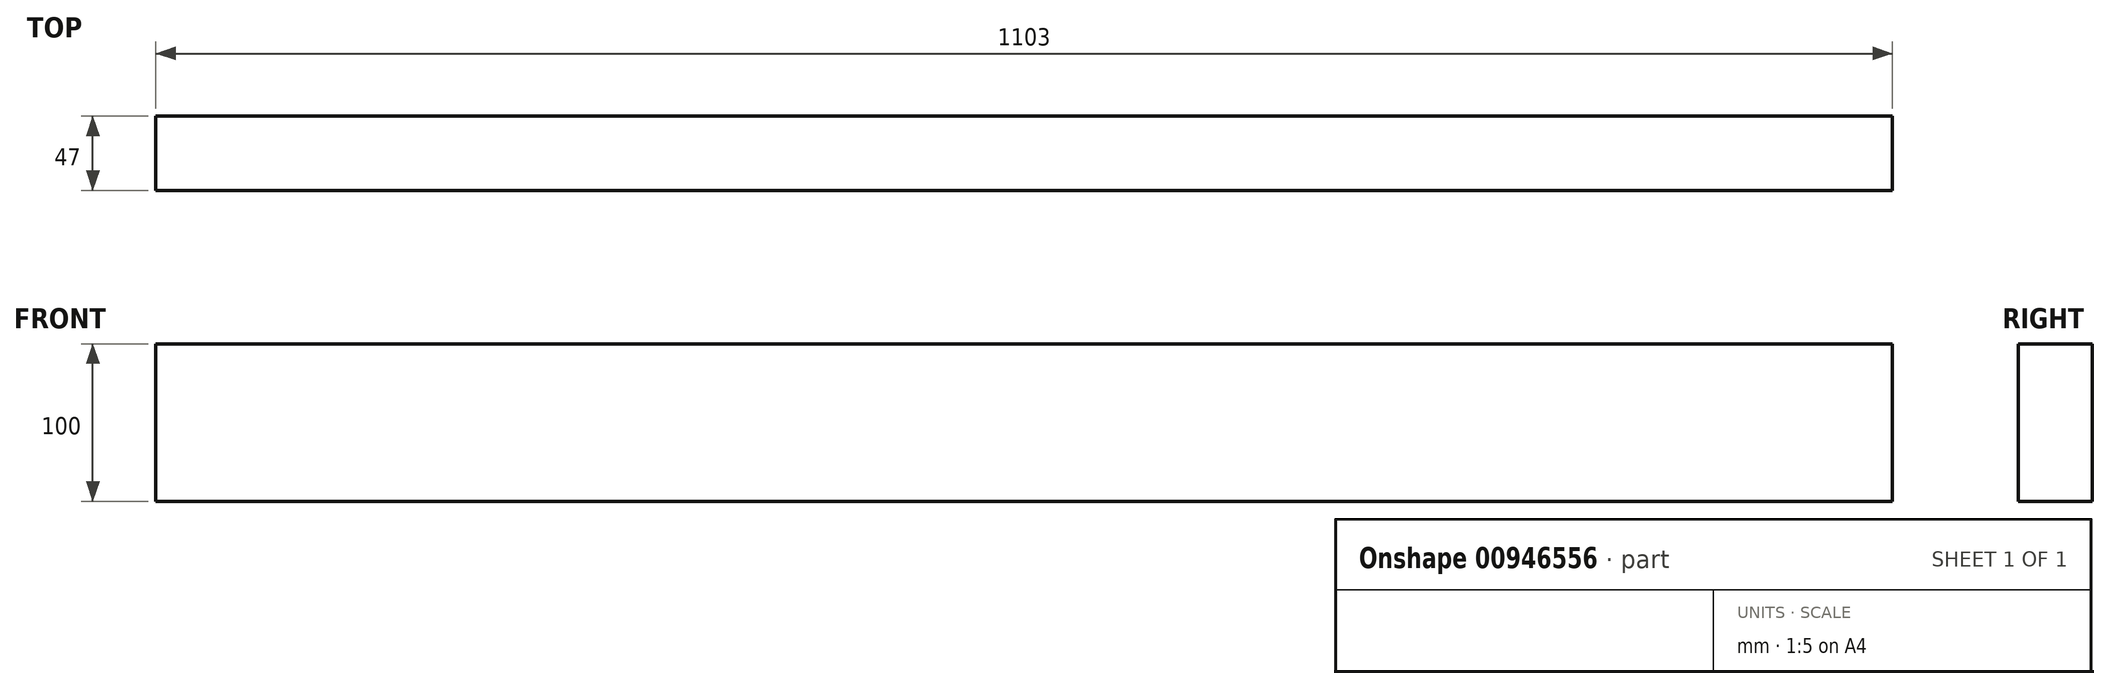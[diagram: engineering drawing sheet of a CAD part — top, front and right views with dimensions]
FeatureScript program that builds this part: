
annotation { "Feature Type Name" : "Feature", "Feature Type Description" : "" }
export const myFeature = defineFeature(function(context is Context, id is Id, definition is map)
    precondition{}
    {
        {
            var Q0;
            Q0=qCreatedBy(makeId("Right.planeOp"),FACE);
            var sketch = newSketch(context, id + "F0", { "sketchPlane" : qUnion([Q0])});
            skLineSegment(sketch, "E0.bottom", {"start": v(0, 0) * mm, "end": v(-47, 0) * mm});
            skLineSegment(sketch, "E0.top", {"start": v(0, 100) * mm, "end": v(-47, 100) * mm});
            skLineSegment(sketch, "E0.left", {"start": v(0, 0) * mm, "end": v(0, 100) * mm});
            skLineSegment(sketch, "E0.right", {"start": v(-47, 0) * mm, "end": v(-47, 100) * mm});
            skSolve(sketch);
        }
        {
            var Q0;
            Q0=qSketchRegion(id+"F0",true);
            extrude(context, id + "F1", {"entities" : qUnion([Q0]), "depth" : 1103 * mm, "offsetDistance" : 25 * mm});
        }
    });
